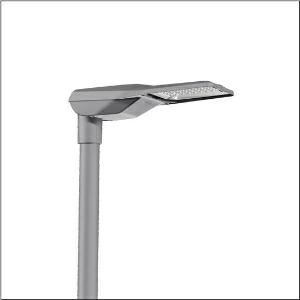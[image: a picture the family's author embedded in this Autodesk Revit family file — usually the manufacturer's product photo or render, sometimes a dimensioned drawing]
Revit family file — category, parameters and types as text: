
# Revit family: streetlight_sl_21_iq_mini___st0_8a_5xe2c31g08hb_2845
name_source: partatom
category: Lighting Fixtures
units: mm (PartAtom-declared; Revit-internal decimal feet)

## family parameters
Cut with Voids When Loaded = No
Host = Face
Light Source = No
Part Type = Normal
Room Calculation Point = No
Round Connector Dimension = Use Diameter
Shared = No

## types (1)
- --- (1 x LED, 9450 lm, 70.9 W, 3000K)
    Apparent Load = 71 VA
    CIE Flux Codes = 38 75 97 100 100
    Color Rendering = 70
    Color Temperature = 3000K
    Default Elevation = 1800 mm
    Description = Streetlight SL 21 iQ mini, mast luminaire, primary light control with lens, of PMMA, primary optical cover: cover, of toughened safety glass, transparent, light distribution: ST0.8a, light emission: direct distribution, primary light characteristic: asymmetric, installation type: post-top, side-entry, LED, High Power LED, rated luminous flux: 9.450lm, luminous efficacy: 133lm/W, light colour: 730, colour temperature: 3000K, control: Street-Remote, Auto-Match, Temp-Guard, Lumen-Switch, Night-Set, Smart-Wire, Light-Fading, Desk-Remote (wireless, voltage-free reading and setting of iQ features in the workshop via application-optimized NFC function/RFID function), optimised constant luminous flux control (CLO 2.0), presetting dimming linear, mains connection: 220..240V, AC, 50/60Hz, start of lifetime: 71W, end of service life: 75W, reduction: 31W, luminaire housing, of diecast aluminium, powder-coated, Siteco® metallic grey (DB 702S), corrosivity category C5 mid according to DIN EN ISO 12944, please order mast flange separately, inclination adjustable: 0°, 5°, 10°, 15°, sealing non-destructively replaceable, multi-level sealing system, length: 628mm, width: 235mm, height: 110mm, mast flange for spigot size: 42mm (side-entry): 5XC10008XM4, 60/48mm (side-entry/post-top): 5XC10108XM2, 76/60mm (side-entry/post-top): 5XC10108XM1, protection rating (complete): IP66, insulation class (complete): insulation class II (safety insulation), certification: CE, ENEC, ENEC+, VDE, impact resistance: IK09, permissible operating ambient temperature for outdoor applications: -40..+50°C, standard-compliant lighting for roads and squares, packaging unit: 1 piece

Light Distribution: ST0.8a
    Height = 110 mm
    Lamp = 1 x LED
    Lamp Light Flux = 9450 lm
    Lamp Power = 70.9 W
    Lamp count = 1
    Length = 625 mm
    Luminous efficacy = 133 lm/W
    Manufacturer = Siteco
    ModVariant = No
    Model = 5XE2C31G08HB
    Number of Poles = 1
    OnlyDefault = Yes
    Power Factor = 1
    Product Name = Streetlight SL 21 iQ mini | ST0.8a
    Product group = mast luminaire | pylon top
    ProductGroupID = 6100
    Protection Class = Protection class II
    Protection Degree = IP 66
    RLX_Detail_Level = 1
    RLX_Emergency_Light_Flux = 0 lm
    RLX_Emergency_Type = 0
    RLX_Emergency_Type_DB = No
    RlxData = <blob elided: 92289 chars, md5=3b454f25>
    Socket = socket
    Standby Power = 0 W
    System Light Flux = 9450 lm
    System Power = 71 W
    Type Comments = factory setting: luminous flux: 100 % | dim-lin: 254 | 711 mA
    Type Image = l_1003519.jpg
    URL = http://relux.com
    VarID = @adj_089735
    Voltage = 0 V
    Weight = 0.00 kg
    Width = 234 mm

## geometry (parser evidence)
native form markers: Blend x4, Sweep x11
no freeform markers — native parametric forms only
